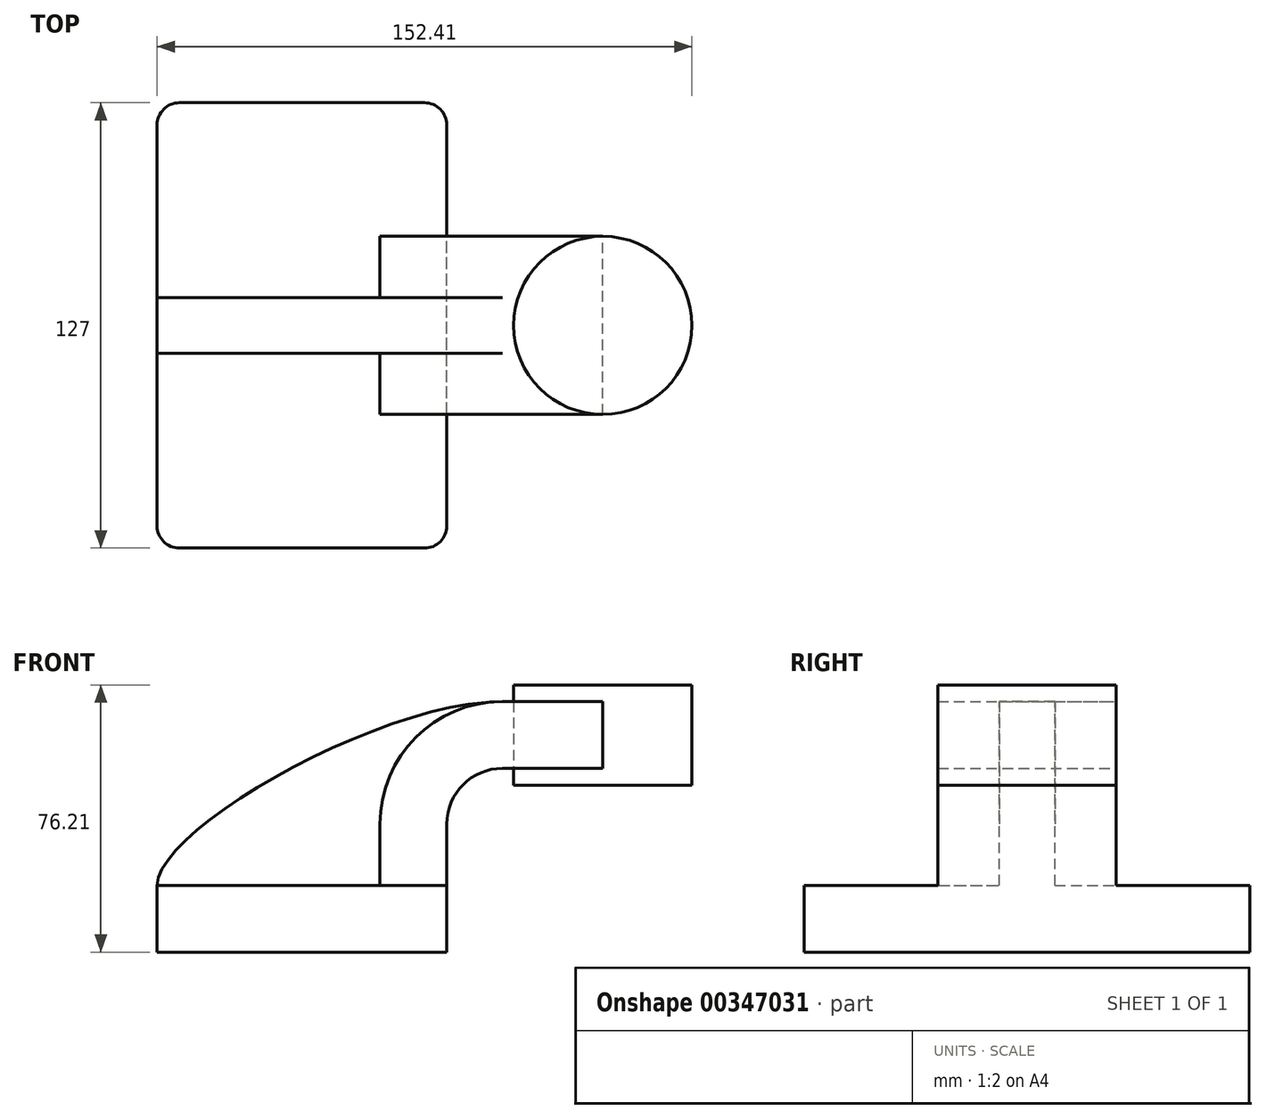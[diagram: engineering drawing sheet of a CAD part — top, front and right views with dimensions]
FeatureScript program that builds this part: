
annotation { "Feature Type Name" : "Feature", "Feature Type Description" : "" }
export const myFeature = defineFeature(function(context is Context, id is Id, definition is map)
    precondition{}
    {
        {
            var Q0;
            Q0=qCreatedBy(makeId("Front.planeOp"),FACE);
            var sketch = newSketch(context, id + "F0", { "sketchPlane" : qUnion([Q0])});
            skLineSegment(sketch, "E0.bottom", {"start": v(41.28, -9.52) * mm, "end": v(-41.28, -9.53) * mm});
            skLineSegment(sketch, "E0.top", {"start": v(41.28, 9.53) * mm, "end": v(-41.28, 9.53) * mm});
            skLineSegment(sketch, "E0.left", {"start": v(41.28, -9.52) * mm, "end": v(41.28, 9.53) * mm});
            skLineSegment(sketch, "E0.right", {"start": v(-41.28, -9.53) * mm, "end": v(-41.28, 9.53) * mm});
            skPoint(sketch, "E0.middle", {"position": v(0, 0) * mm});
            skLineSegment(sketch, "E1.bottom", {"start": v(111.13, 38.1) * mm, "end": v(60.33, 38.1) * mm});
            skLineSegment(sketch, "E1.top", {"start": v(111.13, 66.68) * mm, "end": v(60.33, 66.68) * mm});
            skLineSegment(sketch, "E1.left", {"start": v(111.13, 38.1) * mm, "end": v(111.13, 66.68) * mm});
            skLineSegment(sketch, "E1.right", {"start": v(60.33, 38.1) * mm, "end": v(60.33, 66.68) * mm});
            skPoint(sketch, "E1.middle", {"position": v(85.73, 52.39) * mm});
            skLineSegment(sketch, "E2", {"start": v(41.28, 9.53) * mm, "end": v(41.28, 27) * mm});
            skArc(sketch, "E3", {"start": v(41.27, 27) * mm, "mid": v(45.92, 38.23) * mm, "end": v(57.15, 42.88) * mm});
            skLineSegment(sketch, "E4", {"start": v(57.15, 42.88) * mm, "end": v(85.73, 42.88) * mm});
            skLineSegment(sketch, "E5.0", {"start": v(57.15, 61.93) * mm, "end": v(85.73, 61.93) * mm});
            skArc(sketch, "E5.1", {"start": v(22.22, 27) * mm, "mid": v(32.45, 51.7) * mm, "end": v(57.15, 61.93) * mm});
            skLineSegment(sketch, "E5.2", {"start": v(22.22, 9.53) * mm, "end": v(22.22, 27) * mm});
            skLineSegment(sketch, "E6", {"start": v(85.73, 38.1) * mm, "end": v(85.73, 66.68) * mm});
            skFitSpline(sketch, "E7", {"points": [v(-41.28, 9.53) * mm, v(57.15, 61.93) * mm], "startDerivative": vector(0.44, 48.53) * mm, "endDerivative": vector(104.55, -0.15) * mm});
            skSolve(sketch);
        }
        {
            var Q0;
            Q0=makeQuery(id+"F0.imprint","IMPRINT",FACE,{"disambiguationData":[TD([[makeQuery(id+"F0.imprint","IMPRINT",EDGE,{"derivedFrom":sQuery(id+"F0.wireOp",EDGE,"E0.bottom")}),-1.0]])]});
            extrude(context, id + "F1", {"entities" : qUnion([Q0]), "endBound" : BoundingType.SYMMETRIC, "depth" : 127 * mm});
        }
        {
            var Q0;
            {var subQ1=sQuery(id+"F0.wireOp",EDGE,"E2");Q0=makeQuery(id+"F0.imprint","IMPRINT",FACE,{"disambiguationData":[TD([[makeQuery(id+"F0.imprint","IMPRINT",EDGE,{"derivedFrom":subQ1}),1.0]])]});}
            var Q1;
            {var subQ0=sQuery(id+"F0.wireOp",EDGE,"E4");var subQ1=sQuery(id+"F0.wireOp",EDGE,"E1.right");var subQ2=makeQuery(id+"F0.imprint","INTERSECT",VERTEX,{"derivedFrom":[subQ1,subQ0]});Q1=makeQuery(id+"F0.imprint","IMPRINT",FACE,{"disambiguationData":[TD([[makeQuery(id+"F0.imprint","IMPRINT",EDGE,{"disambiguationData":[TD([[subQ2,-1.0]])],"derivedFrom":subQ1}),-1.0]])]});}
            extrude(context, id + "F2", {"entities" : qUnion([Q0, Q1]), "operationType" : NewBodyOperationType.ADD, "endBound" : BoundingType.SYMMETRIC, "depth" : 50.8 * mm});
        }
        {
            var Q0;
            {var subQ3=sQuery(id+"F0.wireOp",EDGE,"E5.2");Q0=makeQuery(id+"F0.imprint","IMPRINT",FACE,{"disambiguationData":[TD([[makeQuery(id+"F0.imprint","IMPRINT",EDGE,{"derivedFrom":subQ3}),1.0]])]});}
            extrude(context, id + "F3", {"entities" : qUnion([Q0]), "operationType" : NewBodyOperationType.ADD, "endBound" : BoundingType.SYMMETRIC, "depth" : 15.88 * mm});
        }
        {
            var Q0;
            {var subQ0=sQuery(id+"F0.wireOp",EDGE,"E1.left");Q0=makeQuery(id+"F0.imprint","IMPRINT",FACE,{"disambiguationData":[TD([[makeQuery(id+"F0.imprint","IMPRINT",EDGE,{"derivedFrom":subQ0}),1.0]])]});}
            var Q1;
            Q1=sQuery(id+"F0.wireOp",EDGE,"E6");
            revolve(context, id + "F4", {"entities" : qUnion([Q0]), "axis" : qUnion([Q1]), "revolveType" : RevolveType.FULL});
        }
        {
            var Q0;
            Q0=makeQuery(id+"F1.opExtrude","CAP_EDGE",EDGE,{"disambiguationData":[OSD([sQuery(id+"F0.wireOp",EDGE,"E0.left")])],"isStart":false});
            var Q1;
            Q1=makeQuery(id+"F1.opExtrude","CAP_EDGE",EDGE,{"disambiguationData":[OSD([sQuery(id+"F0.wireOp",EDGE,"E0.left")])],"isStart":true});
            var Q2;
            Q2=makeQuery(id+"F1.opExtrude","CAP_EDGE",EDGE,{"disambiguationData":[OSD([sQuery(id+"F0.wireOp",EDGE,"E0.right")])],"isStart":true});
            var Q3;
            Q3=makeQuery(id+"F1.opExtrude","CAP_EDGE",EDGE,{"disambiguationData":[OSD([sQuery(id+"F0.wireOp",EDGE,"E0.right")])],"isStart":false});
            fillet(context, id + "F5", {"entities" : qUnion([Q0, Q1, Q2, Q3]), "radius" : 6.35 * mm, "tangentPropagation" : true, "allowEdgeOverflow" : false});
        }
    });
